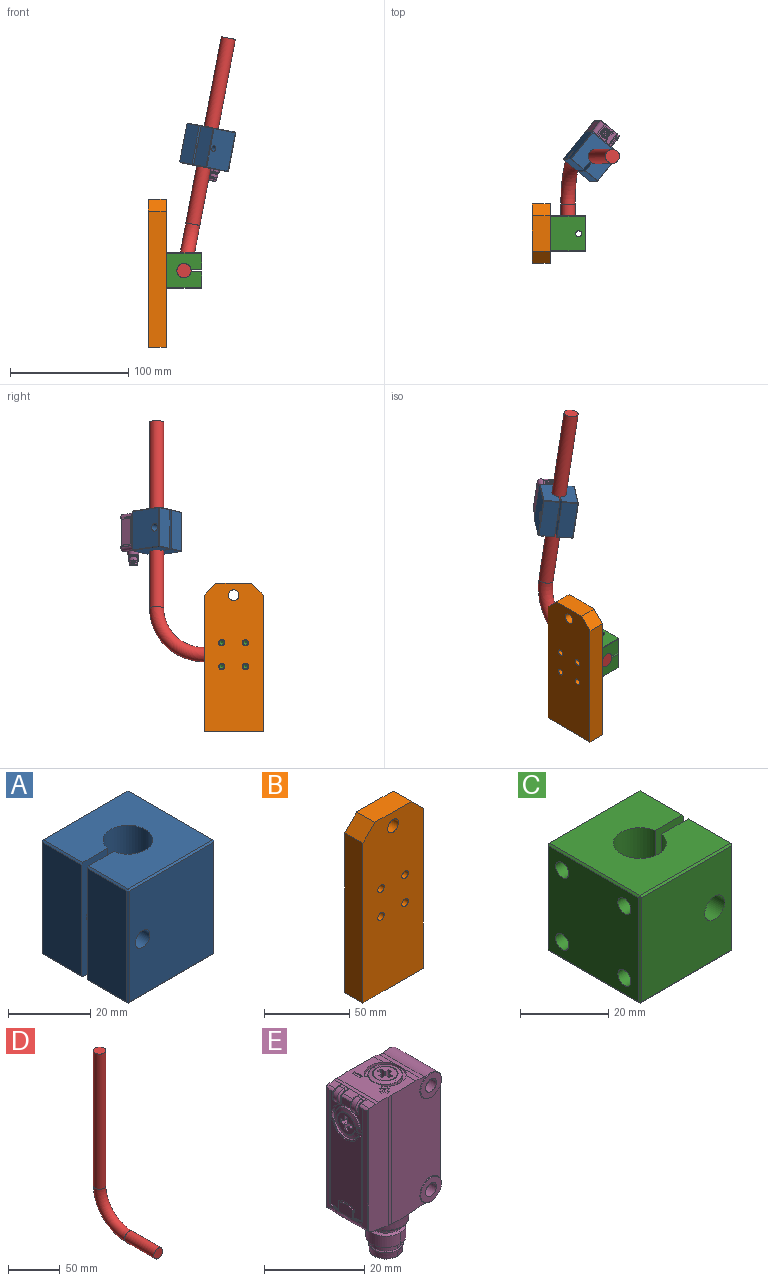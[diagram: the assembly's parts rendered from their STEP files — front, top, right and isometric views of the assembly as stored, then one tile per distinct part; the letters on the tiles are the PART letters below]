
ASSEMBLY  parts=5 mates=5
PART A: 38 faces, bbox 30x30x34 mm
  f0: plane 33x13.5mm, normal (-1,0,0), area 445.5mm2, adj f8,f28,f34,f37
  f1: plane 29x29mm, normal (0,0,1), area 709.1mm2, adj f3,f8,f9,f16,f18,f23,f28,f29
  f2: plane 29x29mm, normal (0,0,-1), area 709.1mm2, adj f3,f8,f9,f20,f25,f31,f35,f37
  f3: cylinder r=6.05mm len=34mm, axis (0,0,1), area 1224.1mm2, adj f1,f2,f8,f9
  f4: plane 33x29mm, normal (1,0,0), area 947.2mm2, adj f11,f13,f23,f24,f30,f31
  f5: plane 33x29mm, normal (0,1,0), area 924.8mm2, adj f15,f18,f19,f24,f25
  f6: plane 33x13.5mm, normal (-1,0,0), area 445.5mm2, adj f9,f16,f19,f20
  f7: plane 33x29mm, normal (0,-1,0), area 937.4mm2, adj f14,f29,f30,f34,f35
  f8: plane 34x9.03mm, normal (0,1,0), area 287.2mm2, adj f0,f1,f2,f3,f14,f28,f37
  f9: plane 34x9.03mm, normal (0,-1,0), area 274.7mm2, adj f1,f2,f3,f6,f15,f16,f20
  f10: cone r=0mm half-angle=59deg, axis (1,0,0), area 5.7mm2, adj f11
  f11: cylinder r=1.25mm len=13.5mm, axis (1,0,0), area 106mm2, adj f4,f10
  f12: cone r=0mm half-angle=59deg, axis (1,0,0), area 5.7mm2, adj f13
  f13: cylinder r=1.25mm len=13.5mm, axis (1,0,0), area 106mm2, adj f4,f12
  f14: cylinder r=2.5mm len=14mm, axis (0,1,0), area 219.9mm2, adj f7,f8
  f15: cylinder r=3.2mm len=14mm, axis (0,-1,0), area 281.5mm2, adj f5,f9
  f16: plane 13.5x0.5mm, normal (-0.71,0,0.71), area 9.5mm2, adj f1,f6,f9,f17
  f17: plane 0.5x0.5mm, normal (-0.58,0.58,0.58), area 0.2mm2, adj f16,f18,f19
  f18: plane 29x0.5mm, normal (0,0.71,0.71), area 20.5mm2, adj f1,f5,f17,f21
  f19: plane 33x0.5mm, normal (-0.71,0.71,0), area 23.3mm2, adj f5,f6,f17,f22
  f20: plane 13.5x0.5mm, normal (-0.71,0,-0.71), area 9.5mm2, adj f2,f6,f9,f22
  f21: plane 0.5x0.5mm, normal (0.58,0.58,0.58), area 0.2mm2, adj f18,f23,f24
  f22: plane 0.5x0.5mm, normal (-0.58,0.58,-0.58), area 0.2mm2, adj f19,f20,f25
  f23: plane 29x0.5mm, normal (0.71,0,0.71), area 20.5mm2, adj f1,f4,f21,f26
  f24: plane 33x0.5mm, normal (0.71,0.71,0), area 23.3mm2, adj f4,f5,f21,f27
  f25: plane 29x0.5mm, normal (0,0.71,-0.71), area 20.5mm2, adj f2,f5,f22,f27
  f26: plane 0.5x0.5mm, normal (0.58,-0.58,0.58), area 0.2mm2, adj f23,f29,f30
  f27: plane 0.5x0.5mm, normal (0.58,0.58,-0.58), area 0.2mm2, adj f24,f25,f31
  f28: plane 13.5x0.5mm, normal (-0.71,0,0.71), area 9.5mm2, adj f0,f1,f8,f32
  f29: plane 29x0.5mm, normal (0,-0.71,0.71), area 20.5mm2, adj f1,f7,f26,f32
  f30: plane 33x0.5mm, normal (0.71,-0.71,0), area 23.3mm2, adj f4,f7,f26,f33
  f31: plane 29x0.5mm, normal (0.71,0,-0.71), area 20.5mm2, adj f2,f4,f27,f33
  f32: plane 0.5x0.5mm, normal (-0.58,-0.58,0.58), area 0.2mm2, adj f28,f29,f34
  f33: plane 0.5x0.5mm, normal (0.58,-0.58,-0.58), area 0.2mm2, adj f30,f31,f35
  f34: plane 33x0.5mm, normal (-0.71,-0.71,0), area 23.3mm2, adj f0,f7,f32,f36
  f35: plane 29x0.5mm, normal (0,-0.71,-0.71), area 20.5mm2, adj f2,f7,f33,f36
  f36: plane 0.5x0.5mm, normal (-0.58,-0.58,-0.58), area 0.2mm2, adj f34,f35,f37
  f37: plane 13.5x0.5mm, normal (-0.71,0,-0.71), area 9.5mm2, adj f0,f2,f8,f36
PART B: 13 faces, bbox 50x15x125 mm
  f0: plane 115x15mm, normal (1,0,0), area 1725mm2, adj f3,f4,f5,f7
  f1: plane 30x15mm, normal (0,0,1), area 450mm2, adj f4,f5,f6,f7
  f2: plane 115x15mm, normal (-1,0,0), area 1725mm2, adj f3,f4,f5,f6
  f3: plane 50x15mm, normal (0,0,-1), area 750mm2, adj f0,f2,f4,f5
  f4: plane 125x50mm, normal (0,-1,0), area 5998.1mm2, adj f0,f1,f2,f3,f6,f7,f8,f9
  f5: plane 125x50mm, normal (0,1,0), area 5998.1mm2, adj f0,f1,f2,f3,f6,f7,f8,f9
  f6: plane 15x10mm, normal (-0.71,0,0.71), area 212.1mm2, adj f1,f2,f4,f5
  f7: plane 15x10mm, normal (0.71,0,0.71), area 212.1mm2, adj f0,f1,f4,f5
  f8: cylinder r=4.5mm len=15mm, axis (0,-1,0), area 424.1mm2, adj f4,f5
  f9: cylinder r=2.65mm len=15mm, axis (0,-1,0), area 249.8mm2, adj f4,f5
  f10: cylinder r=2.65mm len=15mm, axis (0,-1,0), area 249.8mm2, adj f4,f5
  f11: cylinder r=2.65mm len=15mm, axis (0,-1,0), area 249.8mm2, adj f4,f5
  f12: cylinder r=2.65mm len=15mm, axis (0,-1,0), area 249.8mm2, adj f4,f5
PART C: 42 faces, bbox 30x30x30 mm
  f0: cylinder r=6.05mm len=30mm, axis (0,0,1), area 1079.1mm2, adj f6,f7,f8,f9,f18
  f1: plane 29x13.5mm, normal (1,0,0), area 391.5mm2, adj f8,f20,f22,f23
  f2: plane 29x29mm, normal (0,1,0), area 821.4mm2, adj f19,f30,f36,f37,f41
  f3: plane 29x29mm, normal (-1,0,0), area 785.6mm2, adj f11,f13,f15,f17,f28,f29,f35,f36
  f4: plane 29x29mm, normal (0,-1,0), area 808.8mm2, adj f18,f23,f24,f27,f28
  f5: plane 29x13.5mm, normal (1,0,0), area 391.5mm2, adj f9,f31,f37,f38
  f6: plane 29x29mm, normal (0,0,1), area 709.1mm2, adj f0,f8,f9,f22,f27,f35,f38,f41
  f7: plane 29x29mm, normal (0,0,-1), area 709.1mm2, adj f0,f8,f9,f20,f24,f29,f30,f31
  f8: plane 30x9.03mm, normal (0,1,0), area 238.8mm2, adj f0,f1,f6,f7,f18,f20,f22
  f9: plane 30x9.03mm, normal (0,-1,0), area 251.1mm2, adj f0,f5,f6,f7,f19,f31,f38
  f10: cone r=0mm half-angle=59deg, axis (-1,0,0), area 16.2mm2, adj f11
  f11: cylinder r=2.1mm len=14.4mm, axis (-1,0,0), area 190mm2, adj f3,f10
  f12: cone r=0mm half-angle=59deg, axis (-1,0,0), area 16.2mm2, adj f13
  f13: cylinder r=2.1mm len=14.4mm, axis (-1,0,0), area 190mm2, adj f3,f12
  f14: cone r=0mm half-angle=59deg, axis (-1,0,0), area 16.2mm2, adj f15
  f15: cylinder r=2.1mm len=14.4mm, axis (-1,0,0), area 190mm2, adj f3,f14
  f16: cone r=0mm half-angle=59deg, axis (-1,0,0), area 16.2mm2, adj f17
  f17: cylinder r=2.1mm len=14.4mm, axis (-1,0,0), area 190mm2, adj f3,f16
  f18: cylinder r=3.2mm len=14mm, axis (0,-1,0), area 280.4mm2, adj f0,f4,f8
  f19: cylinder r=2.5mm len=14mm, axis (0,-1,0), area 219.9mm2, adj f2,f9
  f20: plane 13.5x0.5mm, normal (0.71,0,-0.71), area 9.5mm2, adj f1,f7,f8,f21
  f21: plane 0.5x0.5mm, normal (0.58,-0.58,-0.58), area 0.2mm2, adj f20,f23,f24
  f22: plane 13.5x0.5mm, normal (0.71,0,0.71), area 9.5mm2, adj f1,f6,f8,f25
  f23: plane 29x0.5mm, normal (0.71,-0.71,0), area 20.5mm2, adj f1,f4,f21,f25
  f24: plane 29x0.5mm, normal (0,-0.71,-0.71), area 20.5mm2, adj f4,f7,f21,f26
  f25: plane 0.5x0.5mm, normal (0.58,-0.58,0.58), area 0.2mm2, adj f22,f23,f27
  f26: plane 0.5x0.5mm, normal (-0.58,-0.58,-0.58), area 0.2mm2, adj f24,f28,f29
  f27: plane 29x0.5mm, normal (0,-0.71,0.71), area 20.5mm2, adj f4,f6,f25,f32
  f28: plane 29x0.5mm, normal (-0.71,-0.71,0), area 20.5mm2, adj f3,f4,f26,f32
  f29: plane 29x0.5mm, normal (-0.71,0,-0.71), area 20.5mm2, adj f3,f7,f26,f33
  f30: plane 29x0.5mm, normal (0,0.71,-0.71), area 20.5mm2, adj f2,f7,f33,f34
  f31: plane 13.5x0.5mm, normal (0.71,0,-0.71), area 9.5mm2, adj f5,f7,f9,f34
  f32: plane 0.5x0.5mm, normal (-0.58,-0.58,0.58), area 0.2mm2, adj f27,f28,f35
  f33: plane 0.5x0.5mm, normal (-0.58,0.58,-0.58), area 0.2mm2, adj f29,f30,f36
  f34: plane 0.5x0.5mm, normal (0.58,0.58,-0.58), area 0.2mm2, adj f30,f31,f37
  f35: plane 29x0.5mm, normal (-0.71,0,0.71), area 20.5mm2, adj f3,f6,f32,f39
  f36: plane 29x0.5mm, normal (-0.71,0.71,0), area 20.5mm2, adj f2,f3,f33,f39
  f37: plane 29x0.5mm, normal (0.71,0.71,0), area 20.5mm2, adj f2,f5,f34,f40
  f38: plane 13.5x0.5mm, normal (0.71,0,0.71), area 9.5mm2, adj f5,f6,f9,f40
  f39: plane 0.5x0.5mm, normal (-0.58,0.58,0.58), area 0.2mm2, adj f35,f36,f41
  f40: plane 0.5x0.5mm, normal (0.58,0.58,0.58), area 0.2mm2, adj f37,f38,f41
  f41: plane 29x0.5mm, normal (0,0.71,0.71), area 20.5mm2, adj f2,f6,f39,f40
PART D: 5 faces, bbox 12x89.8x209.8 mm
  f0: plane 12x12mm, normal (0,-1,0), area 113.1mm2, adj f2
  f1: plane 12x12mm, normal (0,0,1), area 113.1mm2, adj f4
  f2: cylinder r=6mm len=40mm, axis (0,1,0), area 1508mm2, adj f0,f3
  f3: torus R=40mm, axis (1,0,0), area 2368.7mm2, adj f2,f4
  f4: cylinder r=6mm len=160mm, axis (0,0,1), area 6031.9mm2, adj f1,f3
PART E: 278 faces, bbox 22.2x12.4x43.9 mm
  f0: cylinder r=4.2mm len=8.4mm, axis (0,0,1), area 9.5mm2, adj f1,f3,f4,f21,f22,f23,f24
  f1: plane 8.4x7.8mm, normal (0,0,1), area 14.2mm2, adj f0,f2,f3,f18,f19,f20,f21,f244
  f2: plane 0.6x0.32mm, normal (0.71,0.71,0), area 0.3mm2, adj f1,f3,f4,f18
  f3: cylinder r=4.2mm len=3.42mm, axis (0,0,1), area 2.4mm2, adj f0,f1,f2,f4
  f4: plane 12x10.39mm, normal (0,0,1), area 73.7mm2, adj f0,f2,f3,f5,f6,f7,f8,f9
  f5: plane 0.75x0.3mm, normal (0,1,0), area 0.2mm2, adj f4,f6,f16,f17
  f6: plane 0.7x0.3mm, normal (1,0,0), area 0.2mm2, adj f4,f5,f7,f17
  f7: plane 0.75x0.3mm, normal (0,-1,0), area 0.2mm2, adj f4,f6,f8,f17
  f8: plane 0.75x0.3mm, normal (1,0,0), area 0.2mm2, adj f4,f7,f9,f17
  f9: plane 0.7x0.3mm, normal (0,-1,0), area 0.2mm2, adj f4,f8,f10,f17
  f10: plane 0.75x0.3mm, normal (-1,0,0), area 0.2mm2, adj f4,f9,f11,f17
  f11: plane 0.75x0.3mm, normal (0,-1,0), area 0.2mm2, adj f4,f10,f12,f17
  f12: plane 0.7x0.3mm, normal (-1,0,0), area 0.2mm2, adj f4,f11,f13,f17
  f13: plane 0.75x0.3mm, normal (0,1,0), area 0.2mm2, adj f4,f12,f14,f17
  f14: plane 0.75x0.3mm, normal (-1,0,0), area 0.2mm2, adj f4,f13,f15,f17
  f15: plane 0.7x0.3mm, normal (0,1,0), area 0.2mm2, adj f4,f14,f16,f17
  f16: plane 0.75x0.3mm, normal (1,0,0), area 0.2mm2, adj f4,f5,f15,f17
  f17: plane 2.2x2.2mm, normal (0,0,1), area 2.6mm2, adj f5,f6,f7,f8,f9,f10,f11,f12
  f18: cylinder r=0.2mm len=0.6mm, axis (0,0,1), area 0.2mm2, adj f1,f2,f4,f19
  f19: cylinder r=3.6mm len=3.74mm, axis (0,0,1), area 2.4mm2, adj f1,f4,f18,f20
  f20: cylinder r=0.2mm len=0.6mm, axis (0,0,1), area 0.2mm2, adj f1,f4,f19,f21
  f21: plane 0.6x0.32mm, normal (0.71,-0.71,0), area 0.3mm2, adj f0,f1,f4,f20
  f22: cylinder r=5.84mm len=5.03mm, axis (0,-1,0), area 5.6mm2, adj f0,f4,f23,f62
  f23: plane 11.76x1.31mm, normal (0.25,0,0.97), area 15.1mm2, adj f0,f22,f24,f25,f62,f142
  f24: cylinder r=5.84mm len=5.03mm, axis (0,-1,0), area 5.6mm2, adj f0,f4,f23,f25
  f25: plane 31.53x13.98mm, normal (0.02,1,0), area 377.7mm2, adj f4,f23,f24,f26,f59,f63,f64,f78
  f26: plane 31.38x1mm, normal (0,1,0), area 31.3mm2, adj f4,f25,f27,f59
  f27: plane 31.29x0.05mm, normal (-1,0,0), area 1.6mm2, adj f4,f26,f28,f59
  f28: plane 31.3x5.44mm, normal (-0.02,1,0), area 166.9mm2, adj f4,f27,f29,f40,f41,f45,f56,f59
  f29: cylinder r=1mm len=2.36mm, axis (0,-1,0), area 1.8mm2, adj f28,f30,f39,f40,f55,f56,f57
  f30: plane 28.21x9.39mm, normal (-1,0,0), area 33.7mm2, adj f29,f31,f32,f34,f35,f38,f39,f43
  f31: plane 0.7x0.22mm, normal (0,-0.94,0.35), area 0.2mm2, adj f30,f32,f176,f227
  f32: cylinder r=4.2mm len=8.17mm, axis (1,0,0), area 7.9mm2, adj f30,f31,f33,f34,f166,f172,f176
  f33: plane 3.42x1.97mm, normal (-1,0,0), area 5.1mm2, adj f32,f34,f166,f167,f168,f169
  f34: torus R=1.4mm, axis (0,1,0), area 2.5mm2, adj f30,f32,f33,f35,f169,f170
  f35: cylinder r=1.8mm len=3.22mm, axis (0,-1,0), area 5.4mm2, adj f30,f34,f36,f38
  f36: plane 1.2x0.73mm, normal (0,0,1), area 0.9mm2, adj f35,f37,f170,f171
  f37: cylinder r=0.4mm len=0.88mm, axis (1,0,0), area 0.5mm2, adj f36,f38,f39,f171
  f38: torus R=1.4mm, axis (0,1,0), area 2.5mm2, adj f30,f35,f37,f39
  f39: plane 2.35x2.27mm, normal (0,1,0), area 0.9mm2, adj f29,f30,f37,f38,f40,f171
  f40: plane 11.78x1.75mm, normal (-0.14,0,0.99), area 15.2mm2, adj f28,f29,f39,f41,f42,f43,f159,f164
  f41: cylinder r=4.47mm len=11.81mm, axis (0,-1,0), area 9.3mm2, adj f4,f28,f40,f42
  f42: plane 31.3x5.44mm, normal (-0.02,-1,0), area 166.9mm2, adj f4,f40,f41,f43,f44,f45,f59,f60
  f43: cylinder r=1mm len=2.36mm, axis (0,-1,0), area 1.8mm2, adj f30,f40,f42,f44,f48,f58,f159
  f44: cylinder r=0.2mm len=29.58mm, axis (0,0,1), area 7.8mm2, adj f42,f43,f45,f48
  f45: torus R=76.35mm, axis (-1,0,0), area 29.6mm2, adj f28,f42,f44,f46,f47,f48,f54,f55
  f46: plane 8.39x2.75mm, normal (-1,0,0), area 11.3mm2, adj f45,f47,f49,f50,f51,f52,f53,f54
  f47: cylinder r=0.4mm len=0.64mm, axis (0,0,1), area 0mm2, adj f45,f46,f48,f49
  f48: plane 29.38x1.58mm, normal (-0.97,-0.22,0), area 32.9mm2, adj f43,f44,f45,f47,f49,f58
  f49: plane 2.65x0.47mm, normal (0,0.17,0.98), area 0.5mm2, adj f30,f46,f47,f48,f50,f58
  f50: plane 2.05x0.2mm, normal (0,-1,0), area 0.4mm2, adj f30,f46,f49,f51
  f51: cylinder r=3.7mm len=3.9mm, axis (1,0,0), area 0.8mm2, adj f30,f46,f50,f52
  f52: plane 2.05x0.2mm, normal (0,1,0), area 0.4mm2, adj f30,f46,f51,f53
  f53: plane 2.65x0.47mm, normal (0,-0.17,0.98), area 0.5mm2, adj f30,f46,f52,f54,f55,f57
  f54: cylinder r=0.4mm len=0.64mm, axis (0,0,1), area 0mm2, adj f45,f46,f53,f55
  f55: plane 29.38x1.58mm, normal (-0.97,0.22,0), area 32.9mm2, adj f29,f45,f53,f54,f56,f57
  f56: cylinder r=0.2mm len=29.58mm, axis (0,0,1), area 7.8mm2, adj f28,f29,f45,f55
  f57: plane 27.55x0.12mm, normal (0,-1,0), area 3.2mm2, adj f29,f30,f53,f55
  f58: plane 27.55x0.12mm, normal (0,1,0), area 3.2mm2, adj f30,f43,f48,f49
  f59: torus R=36.05mm, axis (-1,0,0), area 61.3mm2, adj f25,f26,f27,f28,f42,f45,f60,f61
  f60: plane 31.29x0.05mm, normal (-1,0,0), area 1.6mm2, adj f4,f42,f59,f61
  f61: plane 31.38x1mm, normal (0,-1,0), area 31.3mm2, adj f4,f59,f60,f62
  f62: plane 31.53x13.98mm, normal (0.02,-1,0), area 377.7mm2, adj f4,f22,f23,f59,f61,f63,f77,f78
  f63: cylinder r=2.2mm len=11.51mm, axis (0,-1,0), area 7.9mm2, adj f25,f62,f64,f66,f77,f141
  f64: cylinder r=0.1mm len=24.36mm, axis (0,0,1), area 3.7mm2, adj f25,f63,f65,f66,f78
  f65: torus R=75.79mm, axis (-1,0,0), area 1.6mm2, adj f64,f66,f77,f78
  f66: plane 23.72x11.31mm, normal (1,0,0), area 41.3mm2, adj f63,f64,f65,f67,f68,f69,f70,f77
  f67: plane 22.4x1.15mm, normal (0,1,0), area 25.8mm2, adj f66,f68,f70,f71
  f68: plane 10.1x1.15mm, normal (0,0,1), area 11.6mm2, adj f66,f67,f69,f71
  f69: plane 22.4x1.15mm, normal (0,-1,0), area 25.8mm2, adj f66,f68,f70,f71
  f70: plane 10.1x1.15mm, normal (0,0,-1), area 11.6mm2, adj f66,f67,f69,f71
  f71: plane 22.4x10.1mm, normal (1,0,0), area 6.5mm2, adj f67,f68,f69,f70,f72,f73,f74,f75
  f72: plane 9.9x1.1mm, normal (0,0,-1), area 10.9mm2, adj f71,f73,f75,f76
  f73: plane 22.2x1.1mm, normal (0,-1,0), area 24.4mm2, adj f71,f72,f74,f76
  f74: plane 9.9x1.1mm, normal (0,0,1), area 10.9mm2, adj f71,f73,f75,f76
  f75: plane 22.2x1.1mm, normal (0,1,0), area 24.4mm2, adj f71,f72,f74,f76
  f76: plane 22.2x9.9mm, normal (1,0,0), area 219.8mm2, adj f72,f73,f74,f75
  f77: cylinder r=0.1mm len=24.36mm, axis (0,0,1), area 3.7mm2, adj f62,f63,f65,f66,f78
  f78: cylinder r=3mm len=11.8mm, axis (0,-1,0), area 3.5mm2, adj f25,f62,f64,f65,f77,f79,f81,f95
  f79: cylinder r=3mm len=11.8mm, axis (0,-1,0), area 71.3mm2, adj f25,f62,f78,f80,f94,f96
  f80: torus R=2.9mm, axis (0,1,0), area 1.5mm2, adj f79,f81,f82
  f81: torus R=2.9mm, axis (0,1,0), area 1.5mm2, adj f78,f80,f82
  f82: plane 5.8x5.8mm, normal (0,1,0), area 19.1mm2, adj f80,f81,f83,f84
  f83: cylinder r=1.53mm len=3.06mm, axis (0,-1,0), area 9.6mm2, adj f82,f84,f86
  f84: cylinder r=1.53mm len=3.06mm, axis (0,-1,0), area 9.6mm2, adj f82,f83,f85
  f85: cone r=1.23mm half-angle=45deg, axis (0,1,0), area 1.8mm2, adj f84,f86,f88
  f86: cone r=1.23mm half-angle=45deg, axis (0,1,0), area 1.8mm2, adj f83,f85,f87
  f87: cylinder r=1.23mm len=7.4mm, axis (0,-1,0), area 28.6mm2, adj f86,f88,f90
  f88: cylinder r=1.23mm len=7.4mm, axis (0,-1,0), area 28.6mm2, adj f85,f87,f89
  f89: cone r=1.53mm half-angle=45deg, axis (0,-1,0), area 1.8mm2, adj f88,f90,f92
  f90: cone r=1.53mm half-angle=45deg, axis (0,-1,0), area 1.8mm2, adj f87,f89,f91
  f91: cylinder r=1.53mm len=3.06mm, axis (0,-1,0), area 9.6mm2, adj f90,f92,f93
  f92: cylinder r=1.53mm len=3.06mm, axis (0,-1,0), area 9.6mm2, adj f89,f91,f93
  f93: plane 5.8x5.8mm, normal (0,-1,0), area 19.1mm2, adj f91,f92,f94,f95
  f94: torus R=2.9mm, axis (0,1,0), area 1.5mm2, adj f79,f93,f95
  f95: torus R=2.9mm, axis (0,1,0), area 1.5mm2, adj f78,f93,f94
  f96: torus R=36.05mm, axis (-1,0,0), area 20.4mm2, adj f25,f62,f79,f97,f101
  f97: plane 12.3x8.55mm, normal (0,0,-1), area 21.1mm2, adj f25,f59,f62,f96,f98,f101
  f98: cone r=4.95mm half-angle=6deg, axis (0,0,1), area 50.9mm2, adj f97,f99,f100,f101
  f99: torus R=4mm, axis (0,0,-1), area 10.8mm2, adj f98,f100,f101,f102
  f100: torus R=4mm, axis (0,0,-1), area 10.8mm2, adj f98,f99,f101,f102
  f101: cone r=4.95mm half-angle=6deg, axis (0,0,1), area 50.9mm2, adj f96,f97,f98,f99,f100
  f102: plane 8.01x8.01mm, normal (0,0,-1), area 14mm2, adj f99,f100,f103,f104
  f103: cylinder r=3.4mm len=6.8mm, axis (0,0,1), area 10.7mm2, adj f102,f104,f106
  f104: cylinder r=3.4mm len=6.8mm, axis (0,0,1), area 10.7mm2, adj f102,f103,f105
  f105: cone r=3.4mm half-angle=60deg, axis (0,0,-1), area 8.1mm2, adj f104,f106,f108
  f106: cone r=3.4mm half-angle=60deg, axis (0,0,-1), area 8.1mm2, adj f103,f105,f107
  f107: cylinder r=4mm len=8mm, axis (0,0,1), area 34.2mm2, adj f106,f108,f110
  f108: cylinder r=4mm len=8mm, axis (0,0,1), area 34.2mm2, adj f105,f107,f109
  f109: cone r=4mm half-angle=60deg, axis (0,0,1), area 9.9mm2, adj f108,f110,f112
  f110: cone r=4mm half-angle=60deg, axis (0,0,1), area 9.9mm2, adj f107,f109,f111
  f111: cylinder r=3.25mm len=6.5mm, axis (0,0,1), area 10.2mm2, adj f110,f112,f114
  f112: cylinder r=3.25mm len=6.5mm, axis (0,0,1), area 10.2mm2, adj f109,f111,f113
  f113: cone r=3.25mm half-angle=38.7deg, axis (0,0,-1), area 2.9mm2, adj f112,f114,f116
  f114: cone r=3.25mm half-angle=38.7deg, axis (0,0,-1), area 2.9mm2, adj f111,f113,f115
  f115: torus R=3.35mm, axis (0,0,-1), area 0.9mm2, adj f114,f116,f118
  f116: torus R=3.35mm, axis (0,0,-1), area 0.9mm2, adj f113,f115,f117
  f117: cone r=3.45mm half-angle=6.5deg, axis (0,0,1), area 16.3mm2, adj f116,f118,f120
  f118: cone r=3.45mm half-angle=6.5deg, axis (0,0,1), area 16.3mm2, adj f115,f117,f119
  f119: torus R=3.07mm, axis (0,0,-1), area 2.9mm2, adj f118,f120,f121
  f120: torus R=3.07mm, axis (0,0,-1), area 2.9mm2, adj f117,f119,f121
  f121: plane 6.14x6.14mm, normal (0,0,-1), area 3.2mm2, adj f119,f120,f122,f123
  f122: cylinder r=2.9mm len=5.8mm, axis (0,0,1), area 45.6mm2, adj f121,f123,f124
  f123: cylinder r=2.9mm len=5.8mm, axis (0,0,1), area 45.6mm2, adj f121,f122,f124
  f124: plane 5.8x5.8mm, normal (0,0,-1), area 23.3mm2, adj f122,f123,f125,f126,f129,f130,f133,f134
  f125: cylinder r=0.5mm len=4.2mm, axis (0,0,1), area 6.6mm2, adj f124,f126,f128
  f126: cylinder r=0.5mm len=4.2mm, axis (0,0,1), area 6.6mm2, adj f124,f125,f127
  f127: sphere r=0.5mm, area 0.9mm2, adj f126,f128
  f128: sphere r=0.5mm, area 0.9mm2, adj f125,f127
  f129: cylinder r=0.5mm len=4.2mm, axis (0,0,1), area 6.6mm2, adj f124,f130,f132
  f130: cylinder r=0.5mm len=4.2mm, axis (0,0,1), area 6.6mm2, adj f124,f129,f131
  f131: sphere r=0.5mm, area 0.9mm2, adj f130,f132
  f132: sphere r=0.5mm, area 0.9mm2, adj f129,f131
  f133: cylinder r=0.5mm len=4.2mm, axis (0,0,1), area 6.6mm2, adj f124,f134,f136
  f134: cylinder r=0.5mm len=4.2mm, axis (0,0,1), area 6.6mm2, adj f124,f133,f135
  f135: sphere r=0.5mm, area 0.9mm2, adj f134,f136
  f136: sphere r=0.5mm, area 0.9mm2, adj f133,f135
  f137: cylinder r=0.5mm len=4.2mm, axis (0,0,1), area 6.6mm2, adj f124,f138,f140
  f138: cylinder r=0.5mm len=4.2mm, axis (0,0,1), area 6.6mm2, adj f124,f137,f139
  f139: sphere r=0.5mm, area 0.9mm2, adj f138,f140
  f140: sphere r=0.5mm, area 0.9mm2, adj f137,f139
  f141: cylinder r=3mm len=11.8mm, axis (0,-1,0), area 11.1mm2, adj f25,f62,f63,f142,f144,f157
  f142: cylinder r=3mm len=11.8mm, axis (0,-1,0), area 74.6mm2, adj f23,f25,f62,f141,f143,f158
  f143: torus R=2.9mm, axis (0,1,0), area 1.5mm2, adj f142,f144,f145
  f144: torus R=2.9mm, axis (0,1,0), area 1.5mm2, adj f141,f143,f145
  f145: plane 5.8x5.8mm, normal (0,-1,0), area 19.1mm2, adj f143,f144,f146,f147
  f146: cylinder r=1.53mm len=3.06mm, axis (0,-1,0), area 9.6mm2, adj f145,f147,f149
  f147: cylinder r=1.53mm len=3.06mm, axis (0,-1,0), area 9.6mm2, adj f145,f146,f148
  f148: cone r=1.53mm half-angle=45deg, axis (0,-1,0), area 1.8mm2, adj f147,f149,f151
  f149: cone r=1.53mm half-angle=45deg, axis (0,-1,0), area 1.8mm2, adj f146,f148,f150
  f150: cylinder r=1.23mm len=7.4mm, axis (0,-1,0), area 28.6mm2, adj f149,f151,f153
  f151: cylinder r=1.23mm len=7.4mm, axis (0,-1,0), area 28.6mm2, adj f148,f150,f152
  f152: cone r=1.23mm half-angle=45deg, axis (0,1,0), area 1.8mm2, adj f151,f153,f155
  f153: cone r=1.23mm half-angle=45deg, axis (0,1,0), area 1.8mm2, adj f150,f152,f154
  f154: cylinder r=1.53mm len=3.06mm, axis (0,-1,0), area 9.6mm2, adj f153,f155,f156
  f155: cylinder r=1.53mm len=3.06mm, axis (0,-1,0), area 9.6mm2, adj f152,f154,f156
  f156: plane 5.8x5.8mm, normal (0,1,0), area 19.1mm2, adj f154,f155,f157,f158
  f157: torus R=2.9mm, axis (0,1,0), area 1.5mm2, adj f141,f156,f158
  f158: torus R=2.9mm, axis (0,1,0), area 1.5mm2, adj f142,f156,f157
  f159: plane 2.35x2.27mm, normal (0,-1,0), area 0.9mm2, adj f30,f40,f43,f160,f163,f164
  f160: torus R=1.4mm, axis (0,1,0), area 2.5mm2, adj f30,f159,f161,f163
  f161: cylinder r=1.8mm len=3.22mm, axis (0,-1,0), area 5.4mm2, adj f30,f160,f162,f166
  f162: plane 1.2x0.73mm, normal (0,0,1), area 0.9mm2, adj f161,f163,f164,f165
  f163: cylinder r=0.4mm len=0.88mm, axis (1,0,0), area 0.5mm2, adj f159,f160,f162,f164
  f164: plane 2.06x0.66mm, normal (0.94,0,0.34), area 1.2mm2, adj f40,f159,f162,f163,f165,f167
  f165: cylinder r=0.4mm len=0.88mm, axis (1,0,0), area 0.5mm2, adj f162,f164,f166,f167
  f166: torus R=1.4mm, axis (0,1,0), area 2.5mm2, adj f30,f32,f33,f161,f165,f167
  f167: plane 2.35x2.27mm, normal (0,1,0), area 0.9mm2, adj f33,f40,f164,f165,f166,f168
  f168: cylinder r=1mm len=3mm, axis (0,-1,0), area 2.3mm2, adj f33,f40,f167,f169
  f169: plane 2.35x2.27mm, normal (0,-1,0), area 0.9mm2, adj f33,f34,f40,f168,f170,f171
  f170: cylinder r=0.4mm len=0.88mm, axis (1,0,0), area 0.5mm2, adj f34,f36,f169,f171
  f171: plane 2.06x0.66mm, normal (0.94,0,0.34), area 1.2mm2, adj f36,f37,f39,f40,f169,f170
  f172: plane 0.7x0.22mm, normal (0,0.94,0.35), area 0.2mm2, adj f30,f32,f173,f176
  f173: cylinder r=0.17mm len=0.7mm, axis (1,0,0), area 0.1mm2, adj f30,f172,f174,f176
  f174: plane 0.7x0.18mm, normal (0,0.77,-0.64), area 0.2mm2, adj f30,f173,f175,f176
  f175: cylinder r=4.2mm len=1.11mm, axis (1,0,0), area 0.8mm2, adj f30,f174,f176,f222
  f176: plane 8.4x7.85mm, normal (-1,0,0), area 10.2mm2, adj f31,f32,f172,f173,f174,f175,f177,f178
  f177: cone r=3.46mm half-angle=5deg, axis (1,0,0), area 5mm2, adj f176,f178,f181,f212
  f178: cone r=3.46mm half-angle=5deg, axis (1,0,0), area 5mm2, adj f176,f177,f179,f180
  f179: plane 1.59x0.82mm, normal (0,0,-1), area 0.4mm2, adj f176,f178,f180,f183,f184,f186,f213,f214
  f180: torus R=3.36mm, axis (1,0,0), area 1.2mm2, adj f178,f179,f181,f183
  f181: torus R=3.36mm, axis (1,0,0), area 1.2mm2, adj f177,f180,f182,f212
  f182: cone r=2.56mm half-angle=75deg, axis (1,0,0), area 7.5mm2, adj f181,f183,f185,f212
  f183: cone r=2.56mm half-angle=75deg, axis (1,0,0), area 7.5mm2, adj f179,f180,f182,f184
  f184: torus R=2.43mm, axis (1,0,0), area 1mm2, adj f179,f183,f185,f186
  f185: torus R=2.43mm, axis (1,0,0), area 1mm2, adj f182,f184,f186,f212
  f186: plane 5.47x4.87mm, normal (-1,0,0), area 13.7mm2, adj f179,f184,f185,f187,f188,f190,f191,f192
  f187: plane 1.9x0.75mm, normal (0,1,0), area 1.4mm2, adj f186,f188,f189,f211
  f188: cylinder r=0.1mm len=1.9mm, axis (1,0,0), area 0.3mm2, adj f186,f187,f189,f190
  f189: plane 3.4x3.4mm, normal (-1,0,0), area 5.6mm2, adj f187,f188,f190,f191,f192,f193,f194,f195
  f190: plane 1.9x0.93mm, normal (0,0,1), area 1.8mm2, adj f186,f188,f189,f191
  f191: cylinder r=0.2mm len=1.9mm, axis (1,0,0), area 0.6mm2, adj f186,f189,f190,f192
  f192: plane 1.9x0.93mm, normal (0,1,0), area 1.8mm2, adj f186,f189,f191,f193
  f193: cylinder r=0.1mm len=1.9mm, axis (1,0,0), area 0.3mm2, adj f186,f189,f192,f194
  f194: plane 1.9x0.75mm, normal (0,0,1), area 1.4mm2, adj f186,f189,f193,f195
  f195: cylinder r=0.1mm len=1.9mm, axis (1,0,0), area 0.3mm2, adj f186,f189,f194,f196
  f196: plane 1.9x0.93mm, normal (0,-1,0), area 1.8mm2, adj f186,f189,f195,f197
  f197: cylinder r=0.2mm len=1.9mm, axis (1,0,0), area 0.6mm2, adj f186,f189,f196,f198
  f198: plane 1.9x0.93mm, normal (0,0,1), area 1.8mm2, adj f186,f189,f197,f199
  f199: cylinder r=0.1mm len=1.9mm, axis (1,0,0), area 0.3mm2, adj f186,f189,f198,f200
  f200: plane 1.9x0.75mm, normal (0,-1,0), area 1.4mm2, adj f186,f189,f199,f201
  f201: cylinder r=0.1mm len=1.9mm, axis (1,0,0), area 0.3mm2, adj f186,f189,f200,f202
  f202: plane 1.9x0.93mm, normal (0,0,-1), area 1.8mm2, adj f186,f189,f201,f203
  f203: cylinder r=0.2mm len=1.9mm, axis (1,0,0), area 0.6mm2, adj f186,f189,f202,f204
  f204: plane 1.9x0.93mm, normal (0,-1,0), area 1.8mm2, adj f186,f189,f203,f205
  f205: cylinder r=0.1mm len=1.9mm, axis (1,0,0), area 0.3mm2, adj f186,f189,f204,f206
  f206: plane 1.9x0.75mm, normal (0,0,-1), area 1.4mm2, adj f186,f189,f205,f207
  f207: cylinder r=0.1mm len=1.9mm, axis (1,0,0), area 0.3mm2, adj f186,f189,f206,f208
  f208: plane 1.9x0.93mm, normal (0,1,0), area 1.8mm2, adj f186,f189,f207,f209
  f209: cylinder r=0.2mm len=1.9mm, axis (1,0,0), area 0.6mm2, adj f186,f189,f208,f210
  f210: plane 1.9x0.93mm, normal (0,0,-1), area 1.8mm2, adj f186,f189,f209,f211
  f211: cylinder r=0.1mm len=1.9mm, axis (1,0,0), area 0.3mm2, adj f186,f187,f189,f210
  f212: plane 1.59x0.82mm, normal (0,0,1), area 0.4mm2, adj f176,f177,f181,f182,f185,f186,f213,f214
  f213: cylinder r=0.5mm len=1.09mm, axis (0,0,1), area 0.1mm2, adj f179,f186,f212,f214
  f214: plane 1.09x0.92mm, normal (-0.97,-0.26,0), area 1mm2, adj f179,f212,f213,f215,f216,f217,f218,f219
  f215: plane 0.58x0.14mm, normal (0,-0.62,0.79), area 0.1mm2, adj f176,f212,f214,f216
  f216: cylinder r=4.1mm len=0.54mm, axis (1,0,0), area 0mm2, adj f176,f214,f215,f217
  f217: plane 0.81x0.54mm, normal (0,-1,0), area 0.4mm2, adj f176,f214,f216,f218
  f218: cylinder r=4.1mm len=0.54mm, axis (1,0,0), area 0mm2, adj f176,f214,f217,f219
  f219: plane 0.58x0.14mm, normal (0,-0.62,-0.79), area 0.1mm2, adj f176,f179,f214,f218
  f220: cylinder r=3.65mm len=7.13mm, axis (1,0,0), area 6.9mm2, adj f30,f176,f221,f223
  f221: cylinder r=0.1mm len=0.7mm, axis (1,0,0), area 0.1mm2, adj f30,f176,f220,f222
  f222: plane 0.7x0.48mm, normal (0,0,1), area 0.3mm2, adj f30,f175,f176,f221
  f223: cylinder r=0.1mm len=0.7mm, axis (1,0,0), area 0.1mm2, adj f30,f176,f220,f224
  f224: plane 0.7x0.48mm, normal (0,0,1), area 0.3mm2, adj f30,f176,f223,f225
  f225: cylinder r=4.2mm len=1.11mm, axis (1,0,0), area 0.8mm2, adj f30,f176,f224,f226
  f226: plane 0.7x0.18mm, normal (0,-0.77,-0.64), area 0.2mm2, adj f30,f176,f225,f227
  f227: cylinder r=0.17mm len=0.7mm, axis (1,0,0), area 0.1mm2, adj f30,f31,f176,f226
  f228: cylinder r=3.95mm len=7.53mm, axis (-1,0,0), area 1mm2, adj f30,f229,f236,f238
  f229: plane 20.67x8.6mm, normal (-1,0,0), area 150.9mm2, adj f228,f230,f231,f232,f233,f234,f235,f236
  f230: cylinder r=19.7mm len=2.05mm, axis (-1,0,0), area 0.2mm2, adj f30,f229,f231,f237
  f231: plane 1.98x0.1mm, normal (0,1,0), area 0.2mm2, adj f30,f229,f230,f232
  f232: cylinder r=4mm len=4.5mm, axis (-1,0,0), area 0.5mm2, adj f30,f229,f231,f233
  f233: plane 1.98x0.1mm, normal (0,-1,0), area 0.2mm2, adj f30,f229,f232,f234
  f234: cylinder r=19.7mm len=2.05mm, axis (-1,0,0), area 0.2mm2, adj f30,f229,f233,f235
  f235: plane 20.32x0.1mm, normal (0,1,0), area 2mm2, adj f30,f229,f234,f236
  f236: plane 0.54x0.1mm, normal (0,0,1), area 0.1mm2, adj f30,f228,f229,f235
  f237: plane 20.32x0.1mm, normal (0,-1,0), area 2mm2, adj f30,f229,f230,f238
  f238: plane 0.54x0.1mm, normal (0,0,1), area 0.1mm2, adj f30,f228,f229,f237
  f239: plane 2.2x0.3mm, normal (1,0,0), area 0.7mm2, adj f4,f240,f242,f243
  f240: plane 0.7x0.3mm, normal (0,-1,0), area 0.2mm2, adj f4,f239,f241,f243
  f241: plane 2.2x0.3mm, normal (-1,0,0), area 0.7mm2, adj f4,f240,f242,f243
  f242: plane 0.7x0.3mm, normal (0,1,0), area 0.2mm2, adj f4,f239,f241,f243
  f243: plane 2.2x0.7mm, normal (0,0,1), area 1.5mm2, adj f239,f240,f241,f242
  f244: cone r=3.45mm half-angle=5deg, axis (0,0,-1), area 5.2mm2, adj f1,f245,f247
  f245: cone r=3.45mm half-angle=5deg, axis (0,0,-1), area 5.2mm2, adj f1,f244,f246
  f246: torus R=3.35mm, axis (0,0,-1), area 1.3mm2, adj f245,f247,f249
  f247: torus R=3.35mm, axis (0,0,-1), area 1.3mm2, adj f244,f246,f248
  f248: cone r=2.56mm half-angle=75deg, axis (0,0,-1), area 7.9mm2, adj f247,f249,f251
  f249: cone r=2.56mm half-angle=75deg, axis (0,0,-1), area 7.9mm2, adj f246,f248,f250
  f250: torus R=2.43mm, axis (0,0,-1), area 1mm2, adj f249,f251,f252
  f251: torus R=2.43mm, axis (0,0,-1), area 1mm2, adj f248,f250,f252
  f252: plane 4.87x4.87mm, normal (0,0,1), area 13.6mm2, adj f250,f251,f253,f254,f255,f257,f258,f259
  f253: cylinder r=0.2mm len=2mm, axis (0,0,-1), area 0.6mm2, adj f252,f254,f256,f277
  f254: plane 2x0.61mm, normal (0,1,0), area 1.2mm2, adj f252,f253,f255,f256
  f255: cylinder r=0.1mm len=2mm, axis (0,0,-1), area 0.3mm2, adj f252,f254,f256,f258
  f256: plane 3.4x2.77mm, normal (0,0,1), area 5mm2, adj f253,f254,f255,f257,f258,f259,f260,f261
  f257: cylinder r=0.1mm len=2mm, axis (0,0,-1), area 0.3mm2, adj f252,f256,f258,f259
  f258: plane 2x0.75mm, normal (1,0,0), area 1.5mm2, adj f252,f255,f256,f257
  f259: plane 2x0.61mm, normal (0,-1,0), area 1.2mm2, adj f252,f256,f257,f260
  f260: cylinder r=0.2mm len=2mm, axis (0,0,-1), area 0.6mm2, adj f252,f256,f259,f261
  f261: plane 2x0.93mm, normal (1,0,0), area 1.8mm2, adj f252,f256,f260,f262
  f262: cylinder r=0.1mm len=2mm, axis (0,0,-1), area 0.3mm2, adj f252,f256,f261,f263
  f263: plane 2x0.75mm, normal (0,-1,0), area 1.5mm2, adj f252,f256,f262,f264
  f264: cylinder r=0.1mm len=2mm, axis (0,0,-1), area 0.3mm2, adj f252,f256,f263,f265
  f265: plane 2x0.93mm, normal (-1,0,0), area 1.8mm2, adj f252,f256,f264,f266
  f266: cylinder r=0.2mm len=2mm, axis (0,0,-1), area 0.6mm2, adj f252,f256,f265,f267
  f267: plane 2x0.61mm, normal (0,-1,0), area 1.2mm2, adj f252,f256,f266,f268
  f268: cylinder r=0.1mm len=2mm, axis (0,0,-1), area 0.3mm2, adj f252,f256,f267,f269
  f269: plane 2x0.75mm, normal (-1,0,0), area 1.5mm2, adj f252,f256,f268,f270
  f270: cylinder r=0.1mm len=2mm, axis (0,0,-1), area 0.3mm2, adj f252,f256,f269,f271
  f271: plane 2x0.61mm, normal (0,1,0), area 1.2mm2, adj f252,f256,f270,f272
  f272: cylinder r=0.2mm len=2mm, axis (0,0,-1), area 0.6mm2, adj f252,f256,f271,f273
  f273: plane 2x0.93mm, normal (-1,0,0), area 1.8mm2, adj f252,f256,f272,f274
  f274: cylinder r=0.1mm len=2mm, axis (0,0,-1), area 0.3mm2, adj f252,f256,f273,f275
  f275: plane 2x0.75mm, normal (0,1,0), area 1.5mm2, adj f252,f256,f274,f276
  f276: cylinder r=0.1mm len=2mm, axis (0,0,-1), area 0.3mm2, adj f252,f256,f275,f277
  f277: plane 2x0.93mm, normal (1,0,0), area 1.8mm2, adj f252,f253,f256,f276
PLACE A rot(axis=(0.09,0.19,0.98),52deg) t=(-377.38,50.83,-236.29)mm
PLACE B rot(axis=(0,0,1),90deg) t=(-419.75,-14.17,-342.67)mm fixed
PLACE C rot(axis=(1,0,0),90deg) t=(-397.25,-14.17,-340.4)mm
PLACE D rot(axis=(0,1,0),10.8deg) t=(-397.25,-29.17,-340.4)mm
PLACE E rot(axis=(0.09,0.03,1),142.1deg) t=(-371.49,70.47,-253.39)mm
MATE cylindrical C.f13 <-> B.f12  axis (-1,0,0) through (-412.25,-24.17,-350.4)mm
MATE cylindrical C.f0 <-> D.f2  axis (0,-1,0) through (-397.25,-29.17,-340.4)mm
MATE cylindrical C.f17 <-> B.f10  axis (-1,0,0) through (-412.25,-4.17,-330.4)mm
MATE slider E.f25 <-> A.f12  axis (-0.62,-0.78,0.12) through (-374.86,70.04,-223.84)mm
MATE cylindrical A.f3 <-> D.f4  axis (0.19,0,0.98) through (-374.19,50.83,-219.59)mm
